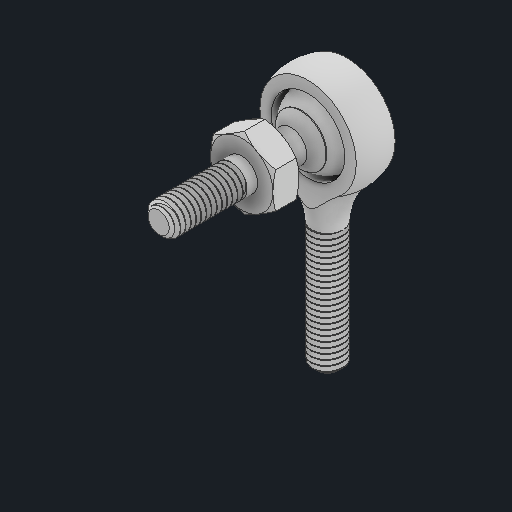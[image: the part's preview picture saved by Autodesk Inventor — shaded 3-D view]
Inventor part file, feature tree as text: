
AUTODESK INVENTOR PART (.ipt)
format: ipt  version: 2023 (Build 270158000, 158)  size: 857,600 bytes
history: native  units: in
note: dims shown in document units (in); Inventor stores cm internally (conversion verified against a paired STEP export)
features: other x1, chamfer x1, revolve x1
ambient origin geometry x8: Origin, YZ Plane, XZ Plane, XY Plane, X Axis, Y Axis, Z Axis, Center Point
bodies: Solid1 (feature_tree), Solid2 (feature_tree), Solid3 (feature_tree)
feature tree (3):
  other  "Cut-Extrude2"
  chamfer  "Chamfer1"  [1 undecoded]
  revolve  "Revolve6"  [1 undecoded]
note: 2 required parameter values undecoded (feature->parameter linkage not recoverable at this tier; creation-order binding heuristic only, values carry confidence <= 0.55)
